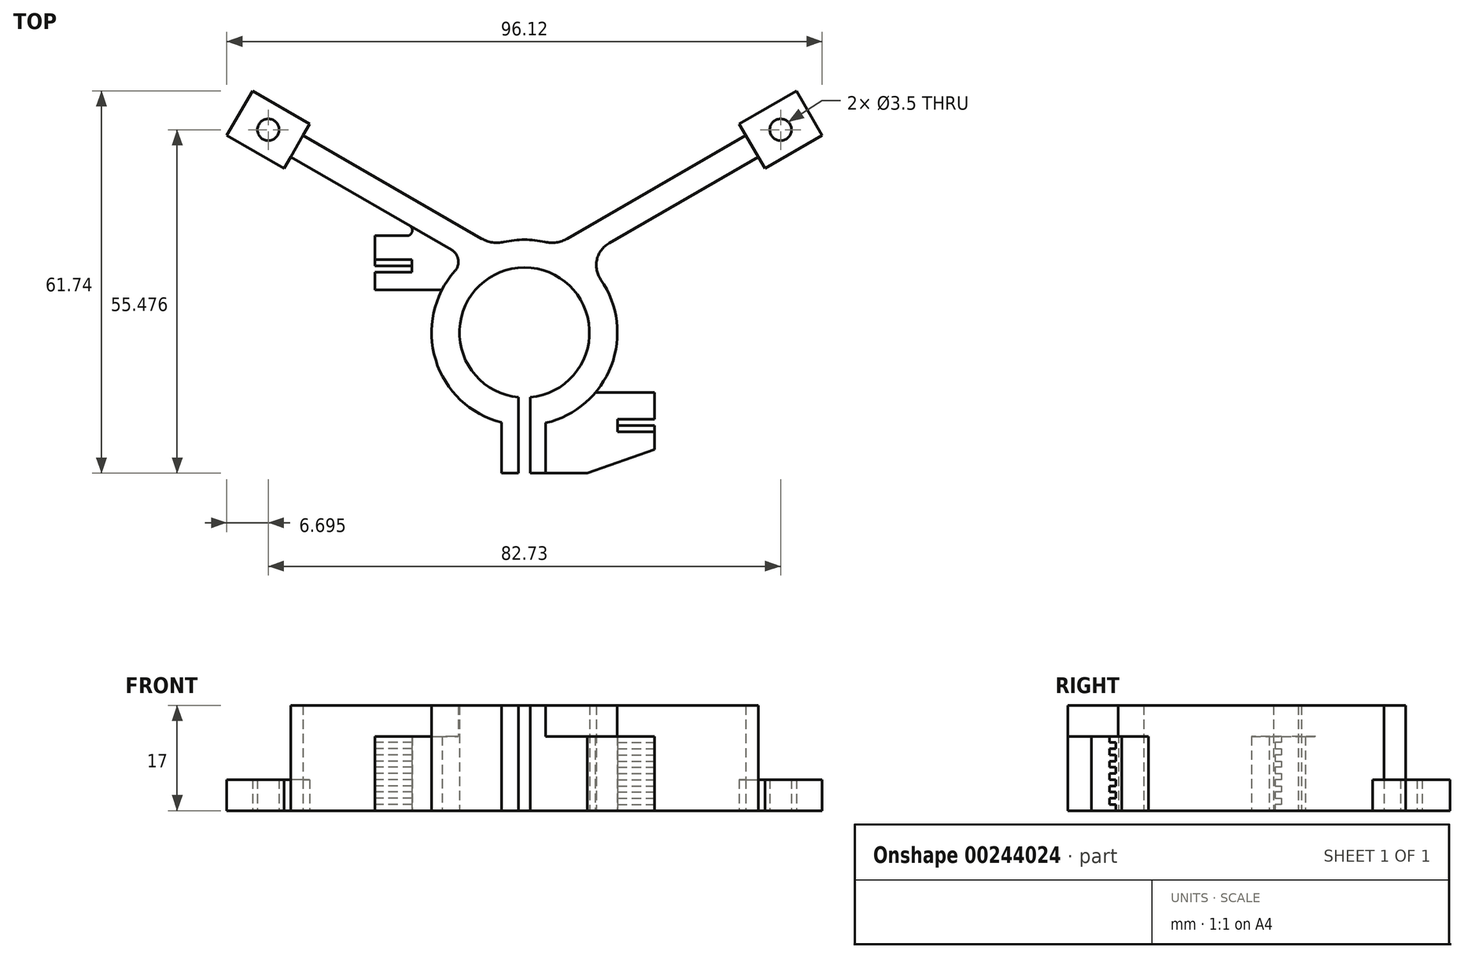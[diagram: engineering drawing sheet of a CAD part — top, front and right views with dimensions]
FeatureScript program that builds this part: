
annotation { "Feature Type Name" : "Feature", "Feature Type Description" : "" }
export const myFeature = defineFeature(function(context is Context, id is Id, definition is map)
    precondition{}
    {
        {
            var Q0;
            Q0=qCreatedBy(makeId("Top.planeOp"),FACE);
            var sketch = newSketch(context, id + "F0", { "sketchPlane" : qUnion([Q0])});
            skArc(sketch, "E0", {"start": v(0.94, -10.46) * mm, "mid": v(0, 10.5) * mm, "end": v(-0.94, -10.46) * mm});
            skArc(sketch, "E1", {"start": v(-13.3, 6.92) * mm, "mid": v(-13.7, -6.13) * mm, "end": v(-3.7, -14.54) * mm});
            skLineSegment(sketch, "E2", {"start": v(6.92, 15.18) * mm, "end": v(35.75, 31.82) * mm});
            skLineSegment(sketch, "E3", {"start": v(35.75, 31.82) * mm, "end": v(34.67, 33.7) * mm});
            skLineSegment(sketch, "E4", {"start": v(34.67, 33.7) * mm, "end": v(43.9, 39.02) * mm});
            skLineSegment(sketch, "E5", {"start": v(43.9, 39.02) * mm, "end": v(48.06, 31.82) * mm});
            skLineSegment(sketch, "E6", {"start": v(48.06, 31.82) * mm, "end": v(38.83, 26.49) * mm});
            skLineSegment(sketch, "E7", {"start": v(38.83, 26.49) * mm, "end": v(37.75, 28.36) * mm});
            skLineSegment(sketch, "E8.MirrorCS", {"start": v(-35.75, 31.82) * mm, "end": v(-34.67, 33.7) * mm});
            skLineSegment(sketch, "E9.MirrorCS", {"start": v(-38.83, 26.49) * mm, "end": v(-37.75, 28.36) * mm});
            skLineSegment(sketch, "E10.MirrorCS", {"start": v(-48.06, 31.82) * mm, "end": v(-38.83, 26.49) * mm});
            skLineSegment(sketch, "E11.MirrorCS", {"start": v(-43.9, 39.02) * mm, "end": v(-48.06, 31.82) * mm});
            skLineSegment(sketch, "E12.MirrorCS", {"start": v(-6.92, 15.18) * mm, "end": v(-35.75, 31.82) * mm});
            skLineSegment(sketch, "E13.MirrorCS", {"start": v(-34.67, 33.7) * mm, "end": v(-43.9, 39.02) * mm});
            skLineSegment(sketch, "E14", {"start": v(-37.75, 28.36) * mm, "end": v(-18.55, 17.27) * mm});
            skCircle(sketch, "E15", {"center": v(41.36, 32.76) * mm, "radius": 1.75 * mm});
            skCircle(sketch, "E16.MirrorC", {"center": v(-41.36, 32.76) * mm, "radius": 1.75 * mm});
            skArc(sketch, "E17.trimOffspring", {"start": v(3.31, 14.63) * mm, "mid": v(0, 15) * mm, "end": v(-3.31, 14.63) * mm});
            skPoint(sketch, "E18.visualSharp", {"position": v(-9.18, 11.86) * mm});
            skPoint(sketch, "E19.visualSharp", {"position": v(-5.08, 14.11) * mm});
            skArc(sketch, "E19.filletArc", {"start": v(-6.92, 15.18) * mm, "mid": v(-5.17, 14.56) * mm, "end": v(-3.31, 14.63) * mm});
            skPoint(sketch, "E20.visualSharp", {"position": v(5.08, 14.11) * mm});
            skArc(sketch, "E20.filletArc", {"start": v(3.31, 14.63) * mm, "mid": v(5.17, 14.56) * mm, "end": v(6.92, 15.18) * mm});
            skLineSegment(sketch, "E21.MirrorCS", {"start": v(-24.16, 10.77) * mm, "end": v(-24.16, 15.64) * mm});
            skLineSegment(sketch, "E22.MirrorCS", {"start": v(-24.16, 10.77) * mm, "end": v(-18.16, 10.77) * mm});
            skLineSegment(sketch, "E23.MirrorCS", {"start": v(-18.16, 10.77) * mm, "end": v(-18.16, 9.77) * mm});
            skLineSegment(sketch, "E24.MirrorCS", {"start": v(-18.16, 9.77) * mm, "end": v(-24.16, 9.77) * mm});
            skLineSegment(sketch, "E25.MirrorCS", {"start": v(-24.16, 6.92) * mm, "end": v(-24.16, 9.77) * mm});
            skLineSegment(sketch, "E26", {"start": v(37.75, 28.36) * mm, "end": v(13.67, 14.46) * mm});
            skLineSegment(sketch, "E27", {"start": v(-24.16, 6.92) * mm, "end": v(-13.3, 6.92) * mm});
            skPoint(sketch, "E28.visualSharp", {"position": v(9.18, 11.86) * mm});
            skArc(sketch, "E28.filletArc", {"start": v(13.67, 14.46) * mm, "mid": v(11.7, 11.79) * mm, "end": v(12.34, 8.53) * mm});
            skLineSegment(sketch, "E29", {"start": v(-24.16, 15.64) * mm, "end": v(-18.98, 15.64) * mm});
            skPoint(sketch, "E30.visualSharp", {"position": v(-15.72, 15.64) * mm});
            skArc(sketch, "E30.filletArc", {"start": v(-18.98, 15.64) * mm, "mid": v(-18.14, 16.29) * mm, "end": v(-18.55, 17.27) * mm});
            skLineSegment(sketch, "E31", {"start": v(0.94, -10.46) * mm, "end": v(0.94, -14.97) * mm});
            skLineSegment(sketch, "E32", {"start": v(0.94, -14.97) * mm, "end": v(0.94, -22.72) * mm});
            skLineSegment(sketch, "E33", {"start": v(0.94, -22.72) * mm, "end": v(4.4, -22.72) * mm});
            skLineSegment(sketch, "E34", {"start": v(4.4, -22.72) * mm, "end": v(10.12, -22.72) * mm});
            skLineSegment(sketch, "E35", {"start": v(10.12, -22.72) * mm, "end": v(21.03, -18.91) * mm});
            skLineSegment(sketch, "E36", {"start": v(21.03, -18.91) * mm, "end": v(21.03, -15) * mm});
            skLineSegment(sketch, "E37", {"start": v(21.03, -15) * mm, "end": v(15.03, -15) * mm});
            skLineSegment(sketch, "E38", {"start": v(15.03, -15) * mm, "end": v(15.03, -14) * mm});
            skLineSegment(sketch, "E39", {"start": v(15.03, -14) * mm, "end": v(21.03, -14) * mm});
            skLineSegment(sketch, "E40", {"start": v(21.03, -14) * mm, "end": v(21.03, -9.71) * mm});
            skLineSegment(sketch, "E41", {"start": v(21.03, -9.71) * mm, "end": v(11.43, -9.71) * mm});
            skLineSegment(sketch, "E42.MirrorCS", {"start": v(-0.94, -10.46) * mm, "end": v(-0.94, -14.97) * mm});
            skLineSegment(sketch, "E43.MirrorCS", {"start": v(-0.94, -14.97) * mm, "end": v(-0.94, -22.72) * mm});
            skLineSegment(sketch, "E44", {"start": v(-0.94, -22.72) * mm, "end": v(-3.7, -22.72) * mm});
            skLineSegment(sketch, "E45", {"start": v(-3.7, -22.72) * mm, "end": v(-3.7, -14.54) * mm});
            skArc(sketch, "E46.trimOffspring", {"start": v(11.43, -9.71) * mm, "mid": v(14.98, -0.74) * mm, "end": v(12.34, 8.53) * mm});
            skSolve(sketch);
        }
        {
            var Q0;
            Q0=makeQuery(id+"F0.imprint","IMPRINT",FACE,{"disambiguationData":[TD([[makeQuery(id+"F0.imprint","IMPRINT",EDGE,{"derivedFrom":sQuery(id+"F0.wireOp",EDGE,"E0")}),-1.0]])]});
            extrude(context, id + "F1", {"entities" : qUnion([Q0]), "depth" : 5 * mm});
        }
        {
            var Q0;
            Q0=makeQuery(id+"F1.opExtrude","CAP_FACE",FACE,{"disambiguationData":[OSD([sQuery(id+"F0.wireOp",EDGE,"E0"),sQuery(id+"F0.wireOp",EDGE,"E1"),sQuery(id+"F0.wireOp",EDGE,"E2"),sQuery(id+"F0.wireOp",EDGE,"E3"),sQuery(id+"F0.wireOp",EDGE,"E4"),sQuery(id+"F0.wireOp",EDGE,"E5"),sQuery(id+"F0.wireOp",EDGE,"E6"),sQuery(id+"F0.wireOp",EDGE,"E7"),sQuery(id+"F0.wireOp",EDGE,"E8.MirrorCS"),sQuery(id+"F0.wireOp",EDGE,"E9.MirrorCS"),sQuery(id+"F0.wireOp",EDGE,"E10.MirrorCS"),sQuery(id+"F0.wireOp",EDGE,"E11.MirrorCS"),sQuery(id+"F0.wireOp",EDGE,"E12.MirrorCS"),sQuery(id+"F0.wireOp",EDGE,"E13.MirrorCS"),sQuery(id+"F0.wireOp",EDGE,"E14"),sQuery(id+"F0.wireOp",EDGE,"E15"),sQuery(id+"F0.wireOp",EDGE,"E16.MirrorC"),sQuery(id+"F0.wireOp",EDGE,"E17.trimOffspring"),sQuery(id+"F0.wireOp",EDGE,"E19.filletArc"),sQuery(id+"F0.wireOp",EDGE,"E20.filletArc"),sQuery(id+"F0.wireOp",EDGE,"E21.MirrorCS"),sQuery(id+"F0.wireOp",EDGE,"E22.MirrorCS"),sQuery(id+"F0.wireOp",EDGE,"E23.MirrorCS"),sQuery(id+"F0.wireOp",EDGE,"E24.MirrorCS"),sQuery(id+"F0.wireOp",EDGE,"E25.MirrorCS"),sQuery(id+"F0.wireOp",EDGE,"E26"),sQuery(id+"F0.wireOp",EDGE,"E27"),sQuery(id+"F0.wireOp",EDGE,"E28.filletArc"),sQuery(id+"F0.wireOp",EDGE,"E29"),sQuery(id+"F0.wireOp",EDGE,"E30.filletArc"),sQuery(id+"F0.wireOp",EDGE,"E31"),sQuery(id+"F0.wireOp",EDGE,"E32"),sQuery(id+"F0.wireOp",EDGE,"E33"),sQuery(id+"F0.wireOp",EDGE,"E34"),sQuery(id+"F0.wireOp",EDGE,"E35"),sQuery(id+"F0.wireOp",EDGE,"E36"),sQuery(id+"F0.wireOp",EDGE,"E37"),sQuery(id+"F0.wireOp",EDGE,"E38"),sQuery(id+"F0.wireOp",EDGE,"E39"),sQuery(id+"F0.wireOp",EDGE,"E40"),sQuery(id+"F0.wireOp",EDGE,"E41"),sQuery(id+"F0.wireOp",EDGE,"E42.MirrorCS"),sQuery(id+"F0.wireOp",EDGE,"E43.MirrorCS"),sQuery(id+"F0.wireOp",EDGE,"E44"),sQuery(id+"F0.wireOp",EDGE,"E45"),sQuery(id+"F0.wireOp",EDGE,"E46.trimOffspring")])],"isStart":false});
            var sketch = newSketch(context, id + "F2", { "sketchPlane" : qUnion([Q0])});
            skLineSegment(sketch, "E47", {"start": v(35.75, 31.82) * mm, "end": v(37.75, 28.36) * mm});
            skLineSegment(sketch, "E48.MirrorCS", {"start": v(-35.75, 31.82) * mm, "end": v(-37.75, 28.36) * mm});
            skSolve(sketch);
        }
        {
            var Q0;
            Q0=makeQuery(id+"F2.imprint","IMPRINT",FACE,{"disambiguationData":[TD([[makeQuery(id+"F2.imprint","IMPRINT",EDGE,{"derivedFrom":sQuery(id+"F2.wireOp",EDGE,"E47")}),-1.0]])]});
            extrude(context, id + "F3", {"entities" : qUnion([Q0]), "operationType" : NewBodyOperationType.ADD, "depth" : 7 * mm});
        }
        {
            var Q0;
            Q0=makeQuery(id+"F3.opExtrude","CAP_FACE",FACE,{"disambiguationData":[OSD([sQuery(id+"F0.wireOp",EDGE,"E0"),sQuery(id+"F0.wireOp",EDGE,"E1"),sQuery(id+"F0.wireOp",EDGE,"E2"),sQuery(id+"F0.wireOp",EDGE,"E12.MirrorCS"),sQuery(id+"F0.wireOp",EDGE,"E14"),sQuery(id+"F0.wireOp",EDGE,"E17.trimOffspring"),sQuery(id+"F0.wireOp",EDGE,"E19.filletArc"),sQuery(id+"F0.wireOp",EDGE,"E20.filletArc"),sQuery(id+"F0.wireOp",EDGE,"E21.MirrorCS"),sQuery(id+"F0.wireOp",EDGE,"E22.MirrorCS"),sQuery(id+"F0.wireOp",EDGE,"E23.MirrorCS"),sQuery(id+"F0.wireOp",EDGE,"E24.MirrorCS"),sQuery(id+"F0.wireOp",EDGE,"E25.MirrorCS"),sQuery(id+"F0.wireOp",EDGE,"E26"),sQuery(id+"F0.wireOp",EDGE,"E27"),sQuery(id+"F0.wireOp",EDGE,"E28.filletArc"),sQuery(id+"F0.wireOp",EDGE,"E29"),sQuery(id+"F0.wireOp",EDGE,"E30.filletArc"),sQuery(id+"F0.wireOp",EDGE,"E31"),sQuery(id+"F0.wireOp",EDGE,"E32"),sQuery(id+"F0.wireOp",EDGE,"E33"),sQuery(id+"F0.wireOp",EDGE,"E34"),sQuery(id+"F0.wireOp",EDGE,"E35"),sQuery(id+"F0.wireOp",EDGE,"E36"),sQuery(id+"F0.wireOp",EDGE,"E37"),sQuery(id+"F0.wireOp",EDGE,"E38"),sQuery(id+"F0.wireOp",EDGE,"E39"),sQuery(id+"F0.wireOp",EDGE,"E40"),sQuery(id+"F0.wireOp",EDGE,"E41"),sQuery(id+"F0.wireOp",EDGE,"E42.MirrorCS"),sQuery(id+"F0.wireOp",EDGE,"E43.MirrorCS"),sQuery(id+"F0.wireOp",EDGE,"E44"),sQuery(id+"F0.wireOp",EDGE,"E45"),sQuery(id+"F0.wireOp",EDGE,"E46.trimOffspring"),sQuery(id+"F2.wireOp",EDGE,"E47"),sQuery(id+"F2.wireOp",EDGE,"E48.MirrorCS")])],"isStart":false});
            var sketch = newSketch(context, id + "F4", { "sketchPlane" : qUnion([Q0])});
            skPoint(sketch, "E49", {"position": v(11.43, -9.71) * mm});
            skLineSegment(sketch, "E50", {"start": v(3.44, -22.72) * mm, "end": v(3.44, -14.6) * mm});
            skArc(sketch, "E51", {"start": v(-11.24, 9.94) * mm, "mid": v(-12.36, 8.5) * mm, "end": v(-13.3, 6.92) * mm});
            skLineSegment(sketch, "E52", {"start": v(-18.55, 17.27) * mm, "end": v(-11.8, 13.38) * mm});
            skPoint(sketch, "E53", {"position": v(-13.3, 6.92) * mm});
            skArc(sketch, "E54.trimOffspring", {"start": v(3.44, -14.6) * mm, "mid": v(7.83, -12.8) * mm, "end": v(11.43, -9.71) * mm});
            skPoint(sketch, "E55.visualSharp", {"position": v(-9.18, 11.86) * mm});
            skArc(sketch, "E55.filletArc", {"start": v(-11.24, 9.94) * mm, "mid": v(-10.7, 11.79) * mm, "end": v(-11.8, 13.38) * mm});
            skSolve(sketch);
        }
        {
            var Q0;
            {var subQ0=sQuery(id+"F4.wireOp",EDGE,"E50");Q0=makeQuery(id+"F4.imprint","IMPRINT",FACE,{"disambiguationData":[TD([[makeQuery(id+"F4.imprint","IMPRINT",EDGE,{"derivedFrom":subQ0}),1.0]])]});}
            extrude(context, id + "F5", {"entities" : qUnion([Q0]), "operationType" : NewBodyOperationType.ADD, "depth" : 5 * mm});
        }
        {
            var Q0;
            {var subQ0=sQuery(id+"F0.wireOp",EDGE,"E36");Q0=makeQuery(id+"F3.boolean.opBoolean","MERGE",FACE,{"derivedFrom":[makeQuery(id+"F1.opExtrude","SWEPT_FACE",FACE,{"disambiguationData":[OSD([subQ0])]}),makeQuery(id+"F3.opExtrude","SWEPT_FACE",FACE,{"disambiguationData":[OSD([subQ0])]})]});}
            var sketch = newSketch(context, id + "F6", { "sketchPlane" : qUnion([Q0])});
            skLineSegment(sketch, "E56", {"start": v(-16, 12) * mm, "end": v(-16, 11) * mm});
            skLineSegment(sketch, "E57", {"start": v(-16, 11) * mm, "end": v(-15, 11) * mm});
            skLineSegment(sketch, "E58", {"start": v(-15, 11) * mm, "end": v(-15, 10) * mm});
            skLineSegment(sketch, "E59", {"start": v(-15, 10) * mm, "end": v(-16, 10) * mm});
            skLineSegment(sketch, "E60.1.0.0", {"start": v(-15, 9) * mm, "end": v(-15, 8) * mm});
            skLineSegment(sketch, "E60.1.0.1", {"start": v(-15, 8) * mm, "end": v(-16, 8) * mm});
            skLineSegment(sketch, "E60.1.0.2", {"start": v(-16, 9) * mm, "end": v(-15, 9) * mm});
            skLineSegment(sketch, "E60.1.0.3", {"start": v(-16, 10) * mm, "end": v(-16, 9) * mm});
            skLineSegment(sketch, "E60.2.0.0", {"start": v(-15, 7) * mm, "end": v(-15, 6) * mm});
            skLineSegment(sketch, "E60.2.0.1", {"start": v(-15, 6) * mm, "end": v(-16, 6) * mm});
            skLineSegment(sketch, "E60.2.0.2", {"start": v(-16, 7) * mm, "end": v(-15, 7) * mm});
            skLineSegment(sketch, "E60.2.0.3", {"start": v(-16, 8) * mm, "end": v(-16, 7) * mm});
            skLineSegment(sketch, "E60.3.0.0", {"start": v(-15, 5) * mm, "end": v(-15, 4) * mm});
            skLineSegment(sketch, "E60.3.0.1", {"start": v(-15, 4) * mm, "end": v(-16, 4) * mm});
            skLineSegment(sketch, "E60.3.0.2", {"start": v(-16, 5) * mm, "end": v(-15, 5) * mm});
            skLineSegment(sketch, "E60.3.0.3", {"start": v(-16, 6) * mm, "end": v(-16, 5) * mm});
            skLineSegment(sketch, "E60.4.0.0", {"start": v(-15, 3) * mm, "end": v(-15, 2) * mm});
            skLineSegment(sketch, "E60.4.0.1", {"start": v(-15, 2) * mm, "end": v(-16, 2) * mm});
            skLineSegment(sketch, "E60.4.0.2", {"start": v(-16, 3) * mm, "end": v(-15, 3) * mm});
            skLineSegment(sketch, "E60.4.0.3", {"start": v(-16, 4) * mm, "end": v(-16, 3) * mm});
            skLineSegment(sketch, "E60.5.0.0", {"start": v(-15, 1) * mm, "end": v(-15, 0) * mm});
            skLineSegment(sketch, "E60.5.0.1", {"start": v(-15, 0) * mm, "end": v(-16, 0) * mm});
            skLineSegment(sketch, "E60.5.0.2", {"start": v(-16, 1) * mm, "end": v(-15, 1) * mm});
            skLineSegment(sketch, "E60.5.0.3", {"start": v(-16, 2) * mm, "end": v(-16, 1) * mm});
            skLineSegment(sketch, "E60.direction1", {"start": v(-15, 10) * mm, "end": v(-15, 8) * mm, "construction": true});
            skSolve(sketch);
        }
        {
            var Q0;
            {var subQ0=sQuery(id+"F6.wireOp",EDGE,"E59");Q0=makeQuery(id+"F6.imprint","IMPRINT",FACE,{"disambiguationData":[TD([[makeQuery(id+"F6.imprint","IMPRINT",EDGE,{"derivedFrom":subQ0}),1.0]])]});}
            var Q1;
            {var subQ0=sQuery(id+"F6.wireOp",EDGE,"E60.1.0.1");Q1=makeQuery(id+"F6.imprint","IMPRINT",FACE,{"disambiguationData":[TD([[makeQuery(id+"F6.imprint","IMPRINT",EDGE,{"derivedFrom":subQ0}),1.0]])]});}
            var Q2;
            {var subQ0=sQuery(id+"F6.wireOp",EDGE,"E56");Q2=makeQuery(id+"F6.imprint","IMPRINT",FACE,{"disambiguationData":[TD([[makeQuery(id+"F6.imprint","IMPRINT",EDGE,{"derivedFrom":subQ0}),1.0]])]});}
            var Q3;
            {var subQ0=sQuery(id+"F6.wireOp",EDGE,"E60.2.0.1");Q3=makeQuery(id+"F6.imprint","IMPRINT",FACE,{"disambiguationData":[TD([[makeQuery(id+"F6.imprint","IMPRINT",EDGE,{"derivedFrom":subQ0}),1.0]])]});}
            var Q4;
            {var subQ0=sQuery(id+"F6.wireOp",EDGE,"E60.3.0.1");Q4=makeQuery(id+"F6.imprint","IMPRINT",FACE,{"disambiguationData":[TD([[makeQuery(id+"F6.imprint","IMPRINT",EDGE,{"derivedFrom":subQ0}),1.0]])]});}
            var Q5;
            {var subQ0=sQuery(id+"F6.wireOp",EDGE,"E60.4.0.1");Q5=makeQuery(id+"F6.imprint","IMPRINT",FACE,{"disambiguationData":[TD([[makeQuery(id+"F6.imprint","IMPRINT",EDGE,{"derivedFrom":subQ0}),1.0]])]});}
            extrude(context, id + "F7", {"entities" : qUnion([Q0, Q1, Q2, Q3, Q4, Q5]), "operationType" : NewBodyOperationType.REMOVE, "oppositeDirection" : true, "depth" : 6 * mm});
        }
        {
            var Q0;
            {var subQ0=sQuery(id+"F0.wireOp",EDGE,"E21.MirrorCS");Q0=makeQuery(id+"F3.boolean.opBoolean","MERGE",FACE,{"derivedFrom":[makeQuery(id+"F1.opExtrude","SWEPT_FACE",FACE,{"disambiguationData":[OSD([subQ0])]}),makeQuery(id+"F3.opExtrude","SWEPT_FACE",FACE,{"disambiguationData":[OSD([subQ0])]})]});}
            var sketch = newSketch(context, id + "F8", { "sketchPlane" : qUnion([Q0])});
            skLineSegment(sketch, "E61", {"start": v(-11.77, 12) * mm, "end": v(-11.77, 11) * mm});
            skLineSegment(sketch, "E62", {"start": v(-11.77, 11) * mm, "end": v(-10.77, 11) * mm});
            skLineSegment(sketch, "E63", {"start": v(-10.77, 11) * mm, "end": v(-10.77, 10) * mm});
            skLineSegment(sketch, "E64", {"start": v(-10.77, 10) * mm, "end": v(-11.77, 10) * mm});
            skLineSegment(sketch, "E65.1.0.0", {"start": v(-11.77, 10) * mm, "end": v(-11.77, 9) * mm});
            skLineSegment(sketch, "E65.1.0.1", {"start": v(-11.77, 9) * mm, "end": v(-10.77, 9) * mm});
            skLineSegment(sketch, "E65.1.0.2", {"start": v(-10.77, 9) * mm, "end": v(-10.77, 8) * mm});
            skLineSegment(sketch, "E65.1.0.3", {"start": v(-10.77, 8) * mm, "end": v(-11.77, 8) * mm});
            skLineSegment(sketch, "E65.2.0.0", {"start": v(-11.77, 8) * mm, "end": v(-11.77, 7) * mm});
            skLineSegment(sketch, "E65.2.0.1", {"start": v(-11.77, 7) * mm, "end": v(-10.77, 7) * mm});
            skLineSegment(sketch, "E65.2.0.2", {"start": v(-10.77, 7) * mm, "end": v(-10.77, 6) * mm});
            skLineSegment(sketch, "E65.2.0.3", {"start": v(-10.77, 6) * mm, "end": v(-11.77, 6) * mm});
            skLineSegment(sketch, "E65.3.0.0", {"start": v(-11.77, 6) * mm, "end": v(-11.77, 5) * mm});
            skLineSegment(sketch, "E65.3.0.1", {"start": v(-11.77, 5) * mm, "end": v(-10.77, 5) * mm});
            skLineSegment(sketch, "E65.3.0.2", {"start": v(-10.77, 5) * mm, "end": v(-10.77, 4) * mm});
            skLineSegment(sketch, "E65.3.0.3", {"start": v(-10.77, 4) * mm, "end": v(-11.77, 4) * mm});
            skLineSegment(sketch, "E65.4.0.0", {"start": v(-11.77, 4) * mm, "end": v(-11.77, 3) * mm});
            skLineSegment(sketch, "E65.4.0.1", {"start": v(-11.77, 3) * mm, "end": v(-10.77, 3) * mm});
            skLineSegment(sketch, "E65.4.0.2", {"start": v(-10.77, 3) * mm, "end": v(-10.77, 2) * mm});
            skLineSegment(sketch, "E65.4.0.3", {"start": v(-10.77, 2) * mm, "end": v(-11.77, 2) * mm});
            skLineSegment(sketch, "E65.5.0.0", {"start": v(-11.77, 2) * mm, "end": v(-11.77, 1) * mm});
            skLineSegment(sketch, "E65.5.0.1", {"start": v(-11.77, 1) * mm, "end": v(-10.77, 1) * mm});
            skLineSegment(sketch, "E65.5.0.2", {"start": v(-10.77, 1) * mm, "end": v(-10.77, 0) * mm});
            skLineSegment(sketch, "E65.5.0.3", {"start": v(-10.77, 0) * mm, "end": v(-11.77, 0) * mm});
            skLineSegment(sketch, "E65.direction1", {"start": v(-11.77, 10) * mm, "end": v(-11.77, 8) * mm, "construction": true});
            skSolve(sketch);
        }
        {
            var Q0;
            {var subQ0=sQuery(id+"F8.wireOp",EDGE,"E61");Q0=makeQuery(id+"F8.imprint","IMPRINT",FACE,{"disambiguationData":[TD([[makeQuery(id+"F8.imprint","IMPRINT",EDGE,{"derivedFrom":subQ0}),1.0]])]});}
            var Q1;
            {var subQ0=sQuery(id+"F8.wireOp",EDGE,"E64");Q1=makeQuery(id+"F8.imprint","IMPRINT",FACE,{"disambiguationData":[TD([[makeQuery(id+"F8.imprint","IMPRINT",EDGE,{"derivedFrom":subQ0}),1.0]])]});}
            var Q2;
            {var subQ0=sQuery(id+"F8.wireOp",EDGE,"E65.1.0.3");Q2=makeQuery(id+"F8.imprint","IMPRINT",FACE,{"disambiguationData":[TD([[makeQuery(id+"F8.imprint","IMPRINT",EDGE,{"derivedFrom":subQ0}),1.0]])]});}
            var Q3;
            {var subQ0=sQuery(id+"F8.wireOp",EDGE,"E65.2.0.3");Q3=makeQuery(id+"F8.imprint","IMPRINT",FACE,{"disambiguationData":[TD([[makeQuery(id+"F8.imprint","IMPRINT",EDGE,{"derivedFrom":subQ0}),1.0]])]});}
            var Q4;
            {var subQ0=sQuery(id+"F8.wireOp",EDGE,"E65.3.0.3");Q4=makeQuery(id+"F8.imprint","IMPRINT",FACE,{"disambiguationData":[TD([[makeQuery(id+"F8.imprint","IMPRINT",EDGE,{"derivedFrom":subQ0}),1.0]])]});}
            var Q5;
            {var subQ0=sQuery(id+"F8.wireOp",EDGE,"E65.4.0.3");Q5=makeQuery(id+"F8.imprint","IMPRINT",FACE,{"disambiguationData":[TD([[makeQuery(id+"F8.imprint","IMPRINT",EDGE,{"derivedFrom":subQ0}),1.0]])]});}
            extrude(context, id + "F9", {"entities" : qUnion([Q0, Q1, Q2, Q3, Q4, Q5]), "operationType" : NewBodyOperationType.REMOVE, "oppositeDirection" : true, "depth" : 6 * mm});
        }
    });
